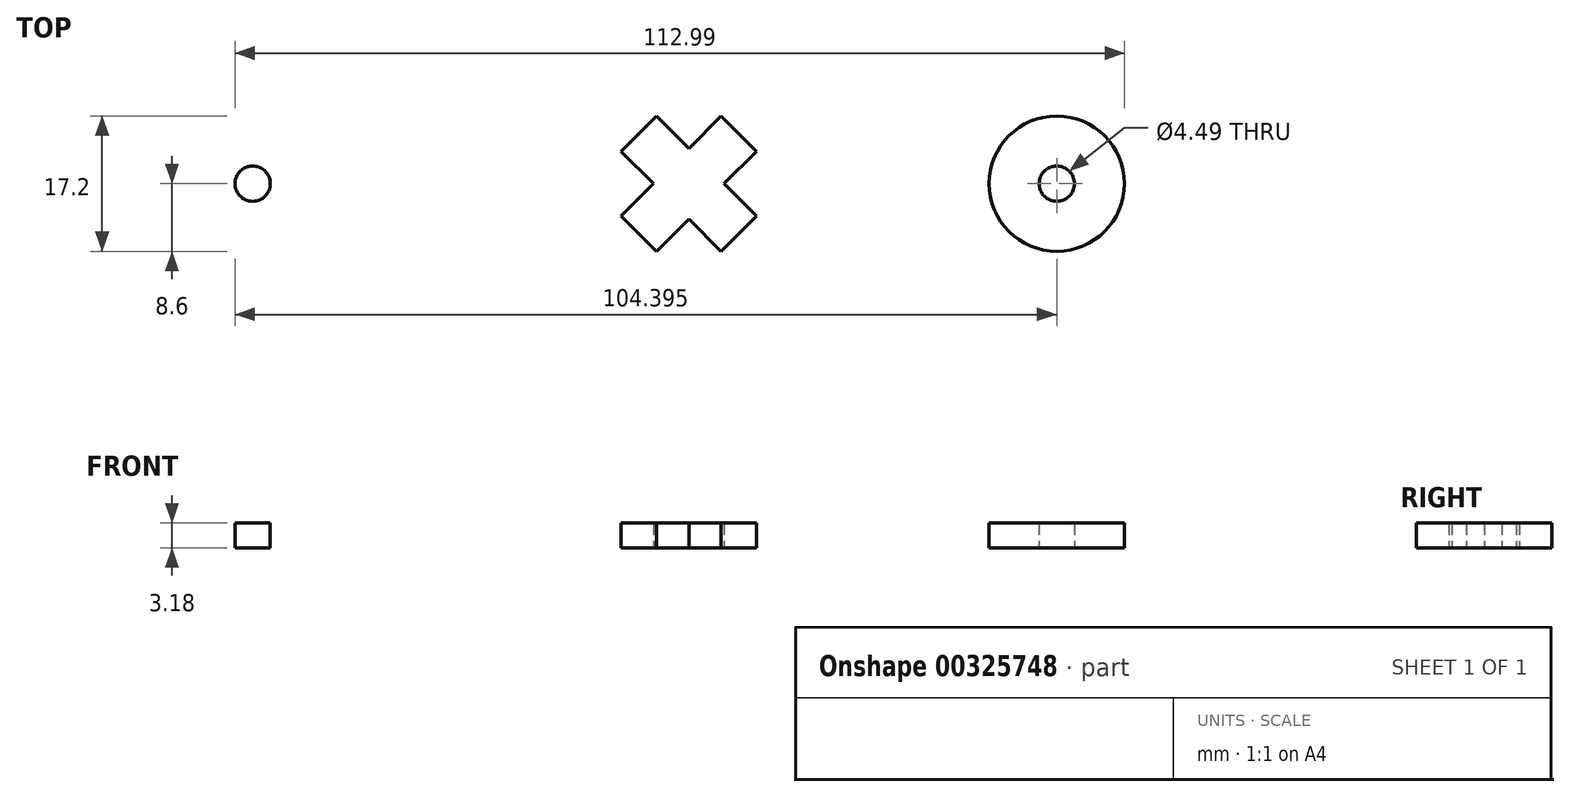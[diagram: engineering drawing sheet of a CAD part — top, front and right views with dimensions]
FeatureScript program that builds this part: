
annotation { "Feature Type Name" : "Feature", "Feature Type Description" : "" }
export const myFeature = defineFeature(function(context is Context, id is Id, definition is map)
    precondition{}
    {
        {
            var Q0;
            Q0=qCreatedBy(makeId("Top.planeOp"),FACE);
            var sketch = newSketch(context, id + "F0", { "sketchPlane" : qUnion([Q0])});
            skLineSegment(sketch, "E0", {"start": v(0, 0) * mm, "end": v(-6.35, 6.35) * mm, "construction": true});
            skLineSegment(sketch, "E1", {"start": v(0, 0) * mm, "end": v(6.35, -6.35) * mm, "construction": true});
            skLineSegment(sketch, "E2", {"start": v(0, 12.1) * mm, "end": v(0, -10.64) * mm, "construction": true});
            skLineSegment(sketch, "E3.MirrorCS", {"start": v(0, 0) * mm, "end": v(6.35, 6.35) * mm, "construction": true});
            skLineSegment(sketch, "E4.MirrorCS", {"start": v(0, 0) * mm, "end": v(-6.35, -6.35) * mm, "construction": true});
            skLineSegment(sketch, "E5.0", {"start": v(0, 4.5) * mm, "end": v(-4.1, 8.6) * mm});
            skLineSegment(sketch, "E6.0", {"start": v(4.5, 0) * mm, "end": v(8.6, 4.1) * mm});
            skLineSegment(sketch, "E7.0", {"start": v(0, -4.5) * mm, "end": v(4.1, -8.6) * mm});
            skLineSegment(sketch, "E8.0", {"start": v(-4.5, 0) * mm, "end": v(-8.6, -4.1) * mm});
            skLineSegment(sketch, "E9.0", {"start": v(-4.5, 0) * mm, "end": v(-8.6, 4.1) * mm});
            skLineSegment(sketch, "E10.0", {"start": v(0, 4.5) * mm, "end": v(4.1, 8.6) * mm});
            skLineSegment(sketch, "E11.0", {"start": v(4.5, 0) * mm, "end": v(8.6, -4.1) * mm});
            skLineSegment(sketch, "E12.0", {"start": v(0, -4.5) * mm, "end": v(-4.1, -8.6) * mm});
            skLineSegment(sketch, "E13", {"start": v(-4.1, 8.6) * mm, "end": v(-8.6, 4.1) * mm});
            skLineSegment(sketch, "E14", {"start": v(4.1, 8.6) * mm, "end": v(8.6, 4.1) * mm});
            skLineSegment(sketch, "E15", {"start": v(8.6, -4.1) * mm, "end": v(4.1, -8.6) * mm});
            skLineSegment(sketch, "E16", {"start": v(-4.1, -8.6) * mm, "end": v(-8.6, -4.1) * mm});
            skSolve(sketch);
        }
        {
            var Q0;
            Q0=makeQuery(id+"F0.imprint","IMPRINT",FACE,{"disambiguationData":[TD([[makeQuery(id+"F0.imprint","IMPRINT",EDGE,{"derivedFrom":sQuery(id+"F0.wireOp",EDGE,"E5.0")}),1.0]])]});
            extrude(context, id + "F1", {"entities" : qUnion([Q0]), "depth" : 3.17 * mm});
        }
        {
            var Q0;
            Q0=qCreatedBy(makeId("Top.planeOp"),FACE);
            var sketch = newSketch(context, id + "F2", { "sketchPlane" : qUnion([Q0])});
            skCircle(sketch, "E17", {"center": v(46.74, 0) * mm, "radius": 8.6 * mm});
            skLineSegment(sketch, "E18", {"start": v(4.1, 8.6) * mm, "end": v(53.65, 8.6) * mm, "construction": true});
            skLineSegment(sketch, "E19", {"start": v(4.1, -8.6) * mm, "end": v(53.65, -8.6) * mm, "construction": true});
            skCircle(sketch, "E20", {"center": v(46.74, 0) * mm, "radius": 2.25 * mm});
            skSolve(sketch);
        }
        {
            var Q0;
            Q0=makeQuery(id+"F2.imprint","IMPRINT",FACE,{"disambiguationData":[TD([[makeQuery(id+"F2.imprint","IMPRINT",EDGE,{"derivedFrom":sQuery(id+"F2.wireOp",EDGE,"E17")}),1.0]])]});
            extrude(context, id + "F3", {"entities" : qUnion([Q0]), "depth" : 3.17 * mm});
        }
        {
            var Q0;
            Q0=qCreatedBy(makeId("Top.planeOp"),FACE);
            var sketch = newSketch(context, id + "F4", { "sketchPlane" : qUnion([Q0])});
            skCircle(sketch, "E21", {"center": v(-55.41, 0) * mm, "radius": 2.25 * mm});
            skSolve(sketch);
        }
        {
            var Q0;
            Q0=makeQuery(id+"F4.imprint","IMPRINT",FACE,{"disambiguationData":[TD([[makeQuery(id+"F4.imprint","IMPRINT",EDGE,{"derivedFrom":sQuery(id+"F4.wireOp",EDGE,"E21")}),1.0]])]});
            extrude(context, id + "F5", {"entities" : qUnion([Q0]), "depth" : 3.17 * mm});
        }
    });
